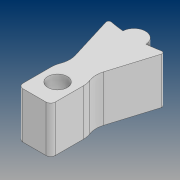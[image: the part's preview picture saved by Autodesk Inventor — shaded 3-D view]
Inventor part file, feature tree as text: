
AUTODESK INVENTOR PART (.ipt)
format: ipt  version: 2021 (Build 250183000, 183)  size: 126,976 bytes
history: native  units: mm
features: fillet x3, extrude x1, sketch x1
ambient origin geometry x8: Origin, YZ Plane, XZ Plane, XY Plane, X Axis, Y Axis, Z Axis, Center Point
bodies: Solid1 (feature_tree)
feature tree (5):
  extrude  "Extrusion1"  Depth=1.0mm
  fillet  "Fillet2"  Radius=10.0mm
  fillet  "Fillet4"  Radius=10.0mm
  fillet  "Fillet5"  Radius=16.5mm
  sketch  "Sketch1"  dims[d1=2.5mm d2=4.2mm d3=10.0mm d4=0.0mm d6=10.0mm d7=16.5mm d8=44.0mm d9=2.96706mm d10=0.5mm d12=10.0mm d13=7.0mm d14=4.75mm d15=1.0mm]
